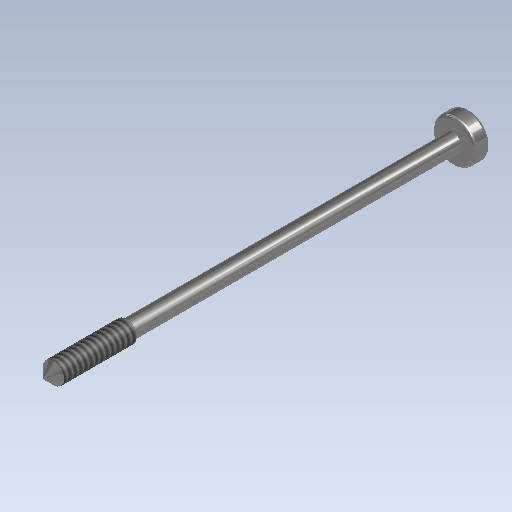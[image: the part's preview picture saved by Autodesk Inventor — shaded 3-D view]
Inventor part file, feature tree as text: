
AUTODESK INVENTOR PART (.ipt)
format: ipt  version: 2020 (Build 240168000, 168)  size: 176,128 bytes
history: native  units: mm
features: sketch x4, chamfer x3, extrude x3, other x1, revolve x1, thread x1, fillet x1, pattern_circular x1
ambient origin geometry x8: Origin, YZ Plane, XZ Plane, XY Plane, X Axis, Y Axis, Z Axis, Center Point
bodies: Body1 (feature_tree)
feature tree (15):
  other  "Твердое тело1"
  revolve  "Вращение1"
  thread  "Резьба1"
  chamfer  "Фаска1"  Distance=20.0mm
  chamfer  "Фаска2"  Distance=1.0mm
  fillet  "Сопряжение1"  Radius=0.8mm
  extrude  "Выдавливание1"  Depth=2.0mm
  extrude  "Выдавливание2"  Depth=0.75mm
  extrude  "Выдавливание3"  Depth=4.0mm
  pattern_circular  "Круговой массив1"  Angle=90.0deg  [1 undecoded]
  chamfer  "Фаска3"  Distance=10.0mm
  sketch  "Эскиз1"
  sketch  "Эскиз2"
  sketch  "Эскиз3"
  sketch  "Эскиз4"
note: 1 required parameter value undecoded (feature->parameter linkage not recoverable at this tier; creation-order binding heuristic only, values carry confidence <= 0.55)
